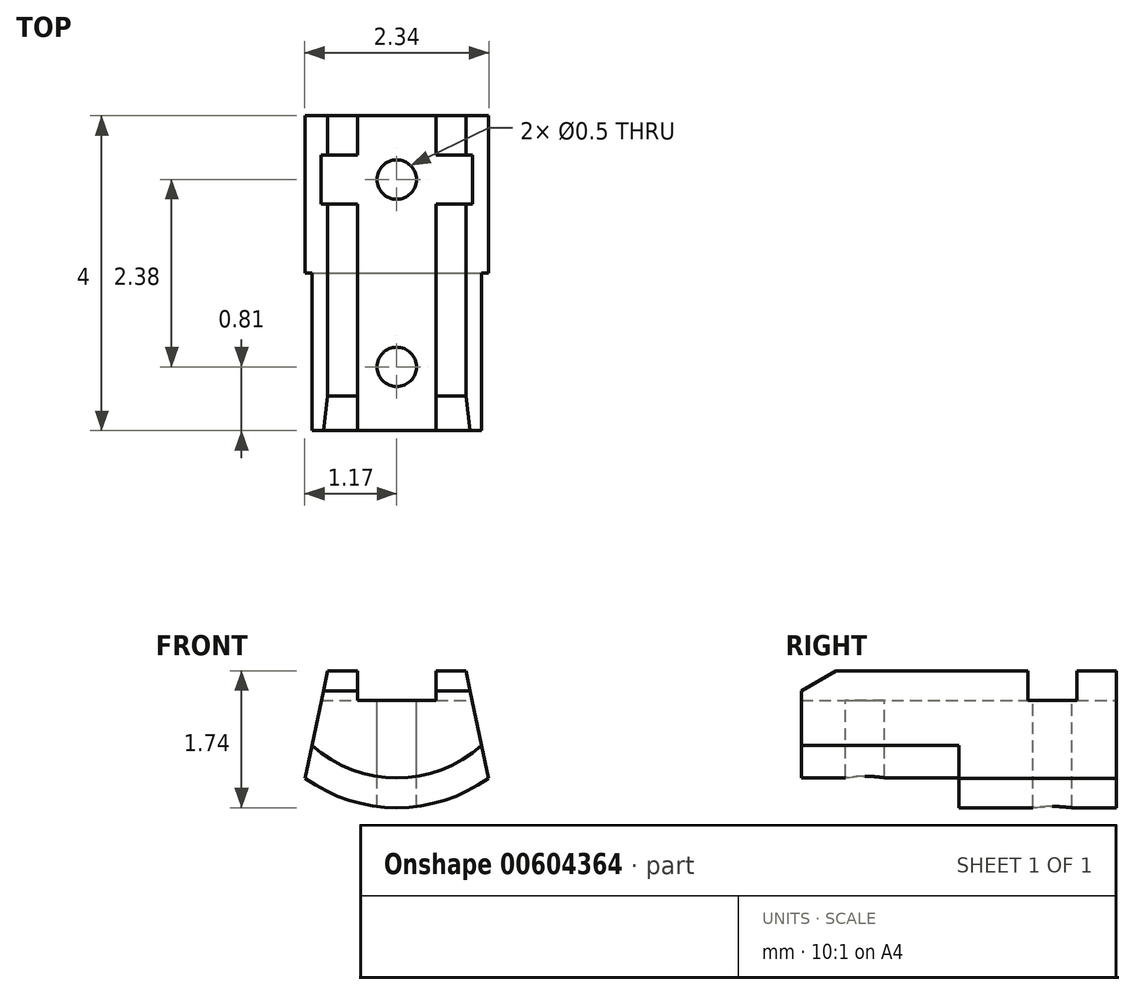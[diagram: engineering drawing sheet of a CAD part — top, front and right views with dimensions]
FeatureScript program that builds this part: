
annotation { "Feature Type Name" : "Feature", "Feature Type Description" : "" }
export const myFeature = defineFeature(function(context is Context, id is Id, definition is map)
    precondition{}
    {
        {
            var Q0;
            Q0=qCreatedBy(makeId("Front.planeOp"),FACE);
            var sketch = newSketch(context, id + "F0", { "sketchPlane" : qUnion([Q0])});
            skCircle(sketch, "E0", {"center": v(0, 0) * mm, "radius": 2 * mm, "construction": true});
            skArc(sketch, "E1", {"start": v(-1.17, -1.63) * mm, "mid": v(0, -2) * mm, "end": v(1.17, -1.63) * mm});
            skLineSegment(sketch, "E2", {"start": v(-1.17, -1.63) * mm, "end": v(-0.88, -0.26) * mm});
            skLineSegment(sketch, "E3", {"start": v(1.17, -1.63) * mm, "end": v(0.88, -0.26) * mm});
            skLineSegment(sketch, "E4", {"start": v(0, -2) * mm, "end": v(0, 2) * mm, "construction": true});
            skPoint(sketch, "E4.startSnap0", {"position": v(0, -2) * mm});
            skLineSegment(sketch, "E5", {"start": v(-0.88, -0.26) * mm, "end": v(-0.5, -0.26) * mm});
            skLineSegment(sketch, "E6.top", {"start": v(-0.5, -0.64) * mm, "end": v(0.5, -0.64) * mm});
            skLineSegment(sketch, "E6.left", {"start": v(-0.5, -0.26) * mm, "end": v(-0.5, -0.64) * mm});
            skLineSegment(sketch, "E6.right", {"start": v(0.5, -0.26) * mm, "end": v(0.5, -0.64) * mm});
            skLineSegment(sketch, "E7.trimOffspring", {"start": v(0.5, -0.26) * mm, "end": v(0.88, -0.26) * mm});
            skSolve(sketch);
        }
        {
            var Q0;
            Q0=makeQuery(id+"F0.imprint","IMPRINT",FACE,{"disambiguationData":[TD([[makeQuery(id+"F0.imprint","IMPRINT",EDGE,{"derivedFrom":sQuery(id+"F0.wireOp",EDGE,"E1")}),1.0]])]});
            extrude(context, id + "F1", {"entities" : qUnion([Q0]), "depth" : 4 * mm, "offsetDistance" : 25 * mm});
        }
        {
            var Q0;
            Q0=qCreatedBy(makeId("Right.planeOp"),FACE);
            var sketch = newSketch(context, id + "F2", { "sketchPlane" : qUnion([Q0])});
            skLineSegment(sketch, "E8.bottom", {"start": v(-0.5, 0) * mm, "end": v(-1.12, 0) * mm});
            skLineSegment(sketch, "E8.top", {"start": v(-0.5, -0.64) * mm, "end": v(-1.12, -0.64) * mm});
            skLineSegment(sketch, "E8.left", {"start": v(-0.5, 0) * mm, "end": v(-0.5, -0.64) * mm});
            skLineSegment(sketch, "E8.right", {"start": v(-1.12, 0) * mm, "end": v(-1.12, -0.64) * mm});
            skLineSegment(sketch, "E9", {"start": v(-3.11, 0) * mm, "end": v(-4, -0.51) * mm});
            skLineSegment(sketch, "E10", {"start": v(-4, -0.51) * mm, "end": v(-4, 0) * mm});
            skLineSegment(sketch, "E11", {"start": v(-4, 0) * mm, "end": v(-3.11, 0) * mm});
            skPoint(sketch, "E12", {"position": v(-3.56, -0.26) * mm});
            skSolve(sketch);
        }
        {
            var Q0;
            Q0 = qSketchRegion(id + "F2", true);
            extrude(context, id + "F3", {"entities" : qUnion([Q0]), "operationType" : NewBodyOperationType.REMOVE, "endBound" : BoundingType.THROUGH_ALL, "oppositeDirection" : true, "depth" : 25 * mm, "offsetDistance" : 25 * mm, "hasSecondDirection" : true, "secondDirectionBound" : SecondDirectionBoundingType.THROUGH_ALL, "secondDirectionOppositeDirection" : false, "secondDirectionDepth" : 25 * mm});
        }
        {
            var Q0;
            Q0=qCreatedBy(makeId("Front.planeOp"),FACE);
            cPlane(context, id + "F4", {"entities" : qUnion([Q0]), "cplaneType" : CPlaneType.OFFSET, "offset" : 2 * mm, "width" : 150 * mm, "height" : 150 * mm});
        }
        {
            var Q0;
            Q0=qCreatedBy(id+"F4.planeOp",FACE);
            var sketch = newSketch(context, id + "F5", { "sketchPlane" : qUnion([Q0])});
            skCircle(sketch, "E13", {"center": v(0, 0) * mm, "radius": 1.62 * mm});
            skCircle(sketch, "E14", {"center": v(0, 0) * mm, "radius": 2.5 * mm});
            skSolve(sketch);
        }
        {
            var Q0;
            Q0 = qSketchRegion(id + "F5", true);
            extrude(context, id + "F6", {"entities" : qUnion([Q0]), "operationType" : NewBodyOperationType.REMOVE, "endBound" : BoundingType.THROUGH_ALL, "depth" : 25 * mm, "offsetDistance" : 25 * mm});
        }
        {
            var Q0;
            Q0=makeQuery(id+"F3.boolean.opBoolean","MERGE",FACE,{"derivedFrom":[makeQuery(id+"F1.opExtrude","SWEPT_FACE",FACE,{"disambiguationData":[OSD([sQuery(id+"F0.wireOp",EDGE,"E6.top")])]}),makeQuery(id+"F3.opExtrude","SWEPT_FACE",FACE,{"disambiguationData":[OSD([sQuery(id+"F2.wireOp",EDGE,"E8.top")])]})]});
            var sketch = newSketch(context, id + "F7", { "sketchPlane" : qUnion([Q0])});
            skPoint(sketch, "E15", {"position": v(0, -0.81) * mm});
            skPoint(sketch, "E16", {"position": v(0, -3.19) * mm});
            skLineSegment(sketch, "E17", {"start": v(0, 0) * mm, "end": v(0, -4) * mm, "construction": true});
            skSolve(sketch);
        }
        {
            var Q0;
            Q0=sQuery(id+"F7.wireOp",VERTEX,"E15");
            var Q1;
            Q1=sQuery(id+"F7.wireOp",VERTEX,"E16");
            var Q2;
            Q2=makeQuery(id+"F1.opExtrude","SWEPT_BODY",BODY,{"disambiguationData":[OSD([sQuery(id+"F0.wireOp",EDGE,"E1"),sQuery(id+"F0.wireOp",EDGE,"E2"),sQuery(id+"F0.wireOp",EDGE,"E3"),sQuery(id+"F0.wireOp",EDGE,"E5"),sQuery(id+"F0.wireOp",EDGE,"E6.top"),sQuery(id+"F0.wireOp",EDGE,"E6.left"),sQuery(id+"F0.wireOp",EDGE,"E6.right"),sQuery(id+"F0.wireOp",EDGE,"E7.trimOffspring")])]});
            hole(context, id + "F8", {"style" : HoleStyle.SIMPLE, "endStyle" : HoleEndStyle.THROUGH, "holeDiameter" : .5 * mm, "majorDiameter" : 5 * mm, "isTappedThrough" : true, "tappedDepth" : 12 * mm, "tapClearance" : 3, "startFromSketch" : true, "locations" : qUnion([Q0, Q1]), "scope" : qUnion([Q2])});
        }
    });
